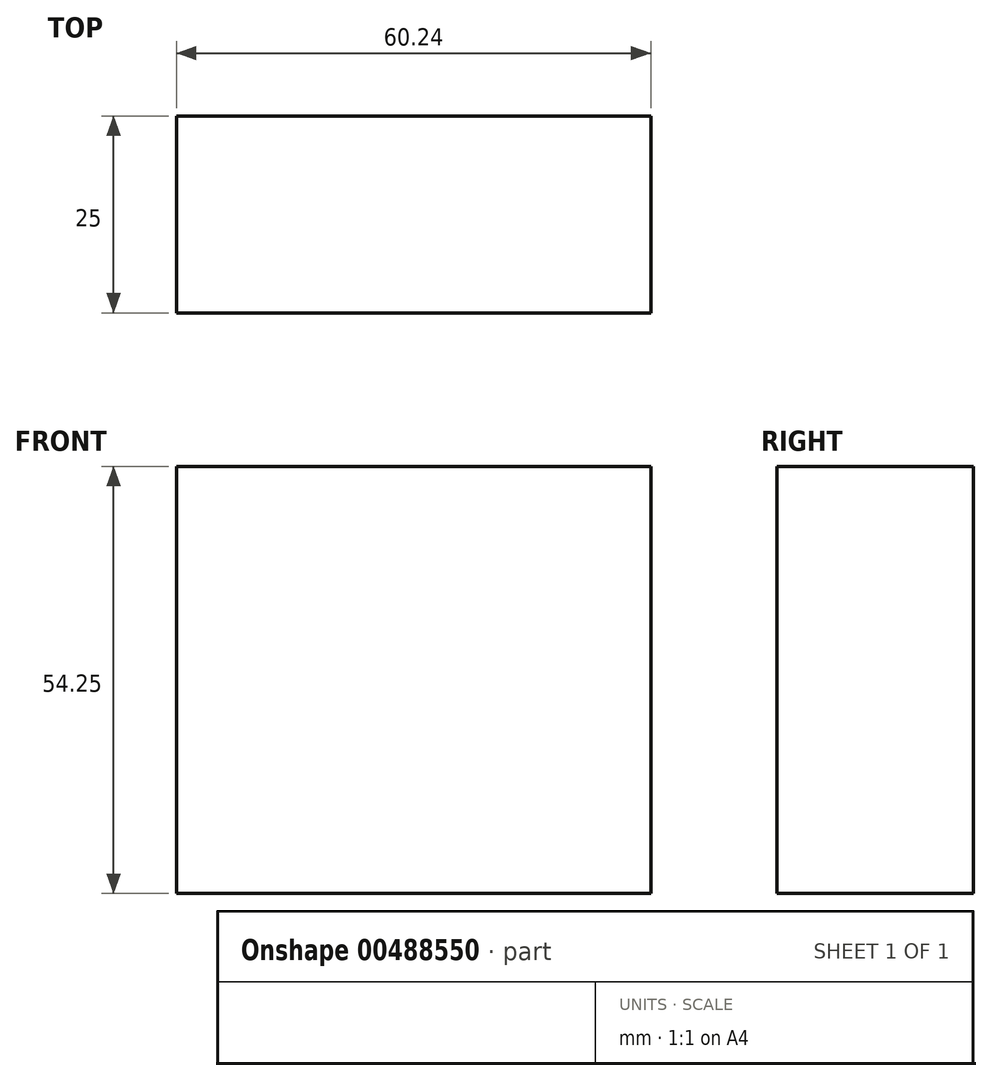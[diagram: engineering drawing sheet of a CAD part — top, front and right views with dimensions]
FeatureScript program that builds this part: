
annotation { "Feature Type Name" : "Feature", "Feature Type Description" : "" }
export const myFeature = defineFeature(function(context is Context, id is Id, definition is map)
    precondition{}
    {
        {
            var Q0;
            Q0=qCreatedBy(makeId("Front.planeOp"),FACE);
            var sketch = newSketch(context, id + "F0", { "sketchPlane" : qUnion([Q0])});
            skLineSegment(sketch, "E0.bottom", {"start": v(-104.9, 13.48) * mm, "end": v(-44.65, 13.48) * mm});
            skLineSegment(sketch, "E0.top", {"start": v(-104.9, 67.73) * mm, "end": v(-44.65, 67.73) * mm});
            skLineSegment(sketch, "E0.left", {"start": v(-104.9, 13.48) * mm, "end": v(-104.9, 67.73) * mm});
            skLineSegment(sketch, "E0.right", {"start": v(-44.65, 13.48) * mm, "end": v(-44.65, 67.73) * mm});
            skPoint(sketch, "E0.middle", {"position": v(-74.77, 40.6) * mm});
            skSolve(sketch);
        }
        {
            var Q0;
            Q0=makeQuery(id+"F0.imprint","IMPRINT",FACE,{"disambiguationData":[TD([[makeQuery(id+"F0.imprint","IMPRINT",EDGE,{"derivedFrom":sQuery(id+"F0.wireOp",EDGE,"E0.bottom")}),1.0]])]});
            extrude(context, id + "F1", {"entities" : qUnion([Q0]), "depth" : 25 * mm});
        }
    });
